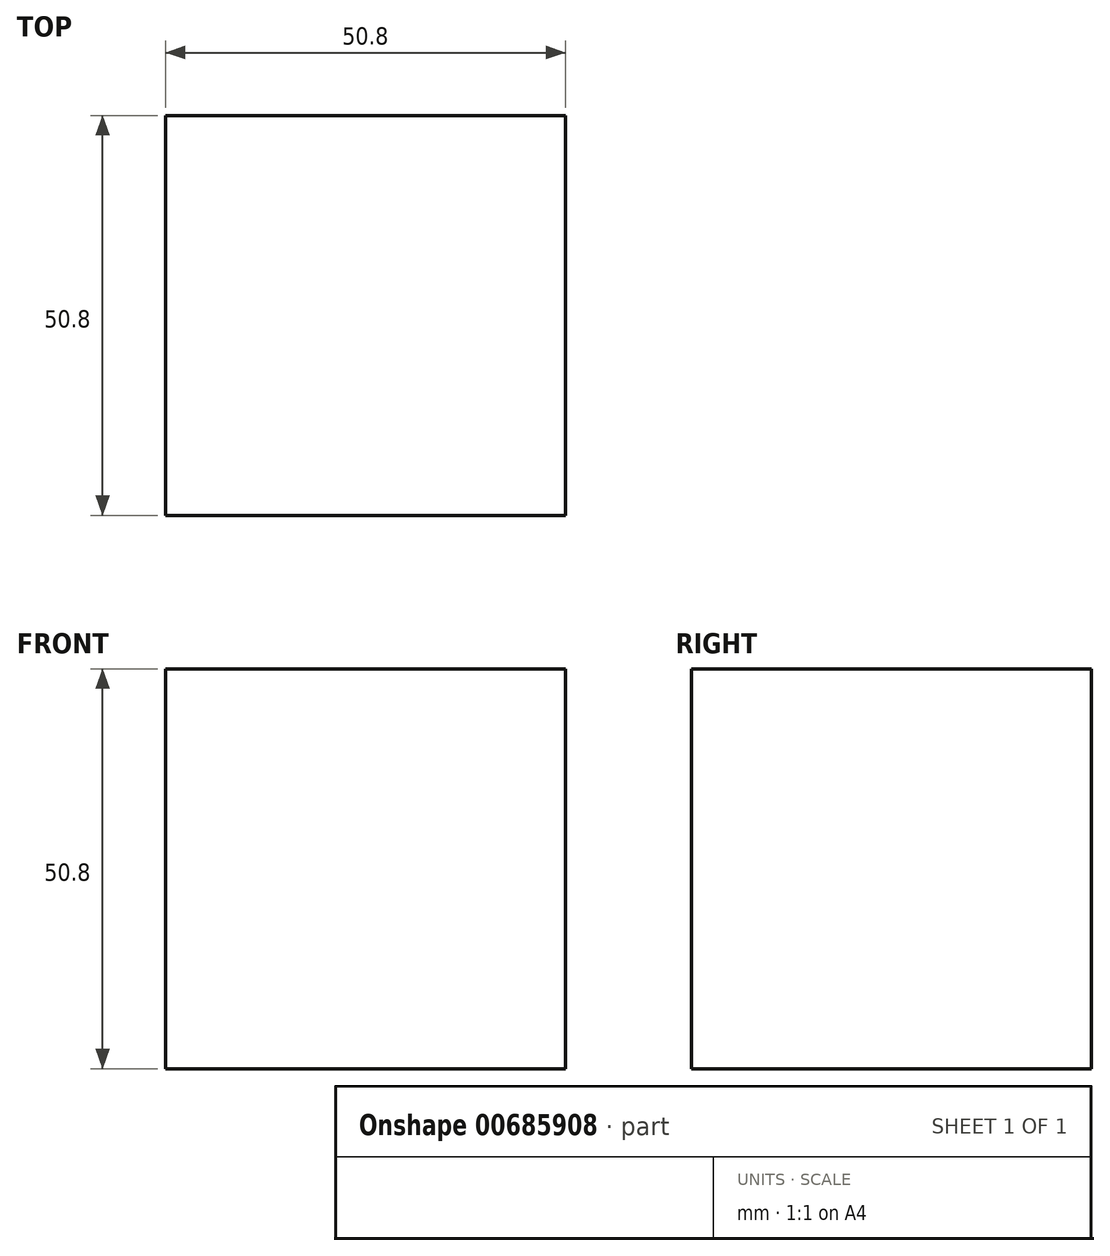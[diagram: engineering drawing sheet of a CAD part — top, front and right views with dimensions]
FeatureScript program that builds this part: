
annotation { "Feature Type Name" : "Feature", "Feature Type Description" : "" }
export const myFeature = defineFeature(function(context is Context, id is Id, definition is map)
    precondition{}
    {
        {
            var Q0;
            Q0=qCreatedBy(makeId("Front.planeOp"),FACE);
            var sketch = newSketch(context, id + "F0", { "sketchPlane" : qUnion([Q0])});
            skLineSegment(sketch, "E0.bottom", {"start": v(0, 0) * mm, "end": v(50.8, 0) * mm});
            skLineSegment(sketch, "E0.top", {"start": v(0, 50.8) * mm, "end": v(50.8, 50.8) * mm});
            skLineSegment(sketch, "E0.left", {"start": v(0, 0) * mm, "end": v(0, 50.8) * mm});
            skLineSegment(sketch, "E0.right", {"start": v(50.8, 0) * mm, "end": v(50.8, 50.8) * mm});
            skSolve(sketch);
        }
        {
            var Q0;
            Q0 = qSketchRegion(id + "F0", true);
            extrude(context, id + "F1", {"entities" : qUnion([Q0]), "depth" : 50.8 * mm, "offsetDistance" : 25.4 * mm});
        }
        {
            var Q0;
            Q0=qCreatedBy(makeId("Front.planeOp"),FACE);
            var sketch = newSketch(context, id + "F2", { "sketchPlane" : qUnion([Q0])});
            skCircle(sketch, "E1", {"center": v(26.07, 25.87) * mm, "radius": 12.7 * mm});
            skSolve(sketch);
        }
        {
            var Q0;
            Q0 = qSketchRegion(id + "F2", true);
            extrude(context, id + "F3", {"entities" : qUnion([Q0]), "operationType" : NewBodyOperationType.REMOVE, "oppositeDirection" : true, "depth" : 25.4 * mm, "offsetDistance" : 25.4 * mm});
        }
    });
